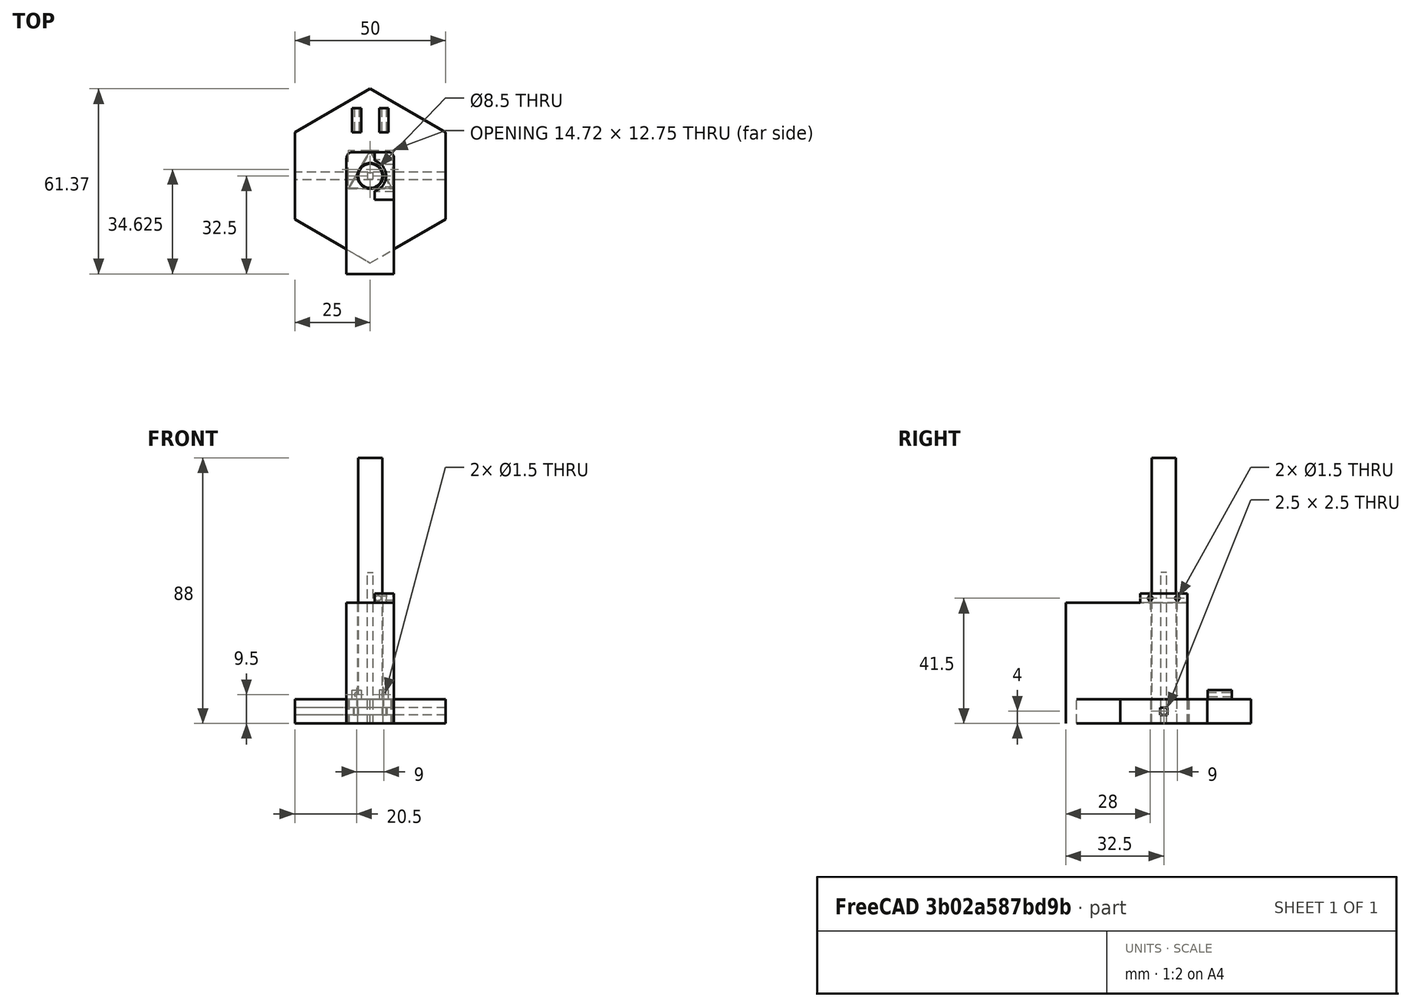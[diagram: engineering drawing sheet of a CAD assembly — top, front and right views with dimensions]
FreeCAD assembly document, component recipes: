
FREECAD ASSEMBLY — COMPONENT RECIPES ("SpringWinder")

This assembly document has 4 components, labeled P0..P3 below (a component is one placed body or linked part). 4 of them carry a construction recipe — the FreeCAD feature program that regenerates the part from scratch, quoted from this document or its linked companion documents; the rest are supplied as boundary geometry only. No exploded tour is included for this assembly.
COMPONENT P0 — recipe-attached ("Handle", modeled in this document).
Construction recipe (the document's own serialized feature program — sketch geometry with constraints, then the solid features built on it; lengths are millimeters unless a unit is written):

FEATURE [Sketcher::SketchObject] Sketch003  label="handle_cylinder_sketch"
  FullyConstrained = true
  MapMode = 5
  Support = -> [XY_Plane004]
  expr: Constraints[18] = <<Specification>>.handle_diameter
  sketch-geometry (7):
    g0: LineSegment StartX=25 StartY=-14.4338 StartZ=0 EndX=25 EndY=14.4338 EndZ=0
    g1: LineSegment StartX=25 StartY=14.4338 StartZ=0 EndX=0 EndY=28.8675 EndZ=0
    g2: LineSegment StartX=0 StartY=28.8675 StartZ=0 EndX=-25 EndY=14.4338 EndZ=0
    g3: LineSegment StartX=-25 StartY=14.4338 StartZ=0 EndX=-25 EndY=-14.4338 EndZ=0
    g4: LineSegment StartX=-25 StartY=-14.4338 StartZ=0 EndX=0 EndY=-28.8675 EndZ=0
    g5: LineSegment StartX=0 StartY=-28.8675 StartZ=0 EndX=25 EndY=-14.4338 EndZ=0
    g6: Circle CenterX=0 CenterY=0 CenterZ=0 NormalX=0 NormalY=0 NormalZ=1 AngleXU=0 Radius=28.8675
  constraints (15):
    c: Coincident(g0,g1)
    c: Coincident(g1,g2)
    c: Coincident(g2,g3)
    c: Coincident(g3,g4)
    c: Coincident(g4,g5)
    c: Coincident(g5,g0)
    c: Equal(g0, g1-g5) x5
    c: PointOnObject(g0,g6)
    c: PointOnObject(g1,g6)
    c: PointOnObject(g2,g6)
    c: PointOnObject(g3,g6)
    c: PointOnObject(g4,g6)
    c: Coincident(g6,g-1)
    c: Symmetric(g3,g0,g-2)
    c: DistanceX(g2,g0) = 50
FEATURE [PartDesign::Pad] Pad002  label="handle_cylinder_pad"
  Direction = (0,0,1)
  Length = 8
  Length2 = 10
  Profile = -> Sketch003
  ReferenceAxis = -> Sketch003 [N_Axis]
  Type = 0
  expr: Length = <<Specification>>.handle_width
FEATURE [PartDesign::CoordinateSystem] Local_CS002  label="handle_pin_hole_cs"
  AttacherType = Attacher::AttachEngine3D
  AttachmentOffset = pos=(25,0,4) rot=(0,0,1;0rad)
  MapMode = 2
  Placement = pos=(25,0,4) rot=(0,0,1;0rad)
  Support = -> [Pad002]
  expr: .AttachmentOffset.Base.x = <<Specification>>.handle_diameter * 0.5
  expr: .AttachmentOffset.Base.z = <<Specification>>.handle_width * 0.5
FEATURE [PartDesign::Plane] DatumPlane001  label="handle_pin_hole_plane"
  Length = 60
  MapMode = 4
  Placement = pos=(25,0,4) rot=(0.57735,0.57735,0.57735;2.0944rad)
  ResizeMode = 0
  Support = -> [Local_CS002]
  Width = 60
FEATURE [Sketcher::SketchObject] Sketch004  label="handle_pin_hole_sketch"
  FullyConstrained = true
  MapMode = 5
  Placement = pos=(25,0,4) rot=(0.57735,0.57735,0.57735;2.0944rad)
  Support = -> [DatumPlane001]
  expr: Constraints[11] = <<Specification>>.fixator_hole_diameter
  sketch-geometry (5):
    g0: LineSegment StartX=-1.25 StartY=-1.25 StartZ=0 EndX=-1.25 EndY=1.25 EndZ=0
    g1: LineSegment StartX=-1.25 StartY=1.25 StartZ=0 EndX=1.25 EndY=1.25 EndZ=0
    g2: LineSegment StartX=1.25 StartY=1.25 StartZ=0 EndX=1.25 EndY=-1.25 EndZ=0
    g3: LineSegment StartX=1.25 StartY=-1.25 StartZ=0 EndX=-1.25 EndY=-1.25 EndZ=0
    g4: GeomPoint X=0 Y=0 Z=0
  constraints (12):
    c: Coincident(g0,g1)
    c: Coincident(g1,g2)
    c: Coincident(g2,g3)
    c: Coincident(g3,g0)
    c: Horizontal(g1)
    c: Horizontal(g3)
    c: Vertical(g0)
    c: Vertical(g2)
    c: Symmetric(g1,g0,g4)
    c: Coincident(g4,g-1)
    c: Equal(g1,g2)
    c: DistanceY(g2,g1) = 2.5
FEATURE [PartDesign::Pocket] Pocket001  label="handle_pin_hole_pocket"
  BaseFeature = -> Pad002
  Direction = (-1,0,0)
  Length = 50
  Length2 = 5
  Profile = -> Sketch004
  ReferenceAxis = -> Sketch004 [N_Axis]
  Type = 1
  expr: Length = <<Specification>>.handle_diameter
FEATURE [Sketcher::SketchObject] Sketch006  label="handle_axis_hole_sketch"
  FullyConstrained = true
  MapMode = 5
  Support = -> [XY_Plane004]
  expr: Constraints[9] = <<Specification>>.inner_radius + <<Parameters>>.big_clearence
  sketch-geometry (4):
    g0: LineSegment StartX=7.36122 StartY=-4.25 StartZ=0 EndX=-9e-16 EndY=8.5 EndZ=0
    g1: LineSegment StartX=-9e-16 StartY=8.5 StartZ=0 EndX=-7.36122 EndY=-4.25 EndZ=0
    g2: LineSegment StartX=-7.36122 StartY=-4.25 StartZ=0 EndX=7.36122 EndY=-4.25 EndZ=0
    g3: Circle CenterX=0 CenterY=0 CenterZ=0 NormalX=0 NormalY=0 NormalZ=1 AngleXU=0 Radius=8.5
  constraints (10):
    c: Coincident(g0,g1)
    c: Coincident(g1,g2)
    c: Coincident(g2,g0)
    c: Equal(g0,g1)
    c: Equal(g0,g2)
    c: PointOnObject(g0,g3)
    c: PointOnObject(g1,g3)
    c: Coincident(g3,g-1)
    c: Symmetric(g1,g0,g-2)
    c: DistanceY(g0,g3) = 4.25
FEATURE [PartDesign::Pocket] Pocket002  label="handle_axis_hole_pocket"
  BaseFeature = -> Pocket001
  Direction = (0,0,-1)
  Length = 5
  Length2 = 5
  Profile = -> Sketch006
  ReferenceAxis = -> Sketch006 [N_Axis]
  Reversed = true
  Type = 1
FEATURE [PartDesign::CoordinateSystem] Local_CS003  label="handle_wire_holder_center_cs"
  AttacherType = Attacher::AttachEngine3D
  AttachmentOffset = pos=(0,14.5,8) rot=(0,0,1;0rad)
  MapMode = 2
  Placement = pos=(0,14.5,8) rot=(0,0,1;0rad)
  Support = -> [Pocket002]
  expr: .AttachmentOffset.Base.y = <<Specification>>.handle_wire_holder_y_offset
  expr: .AttachmentOffset.Base.z = <<Specification>>.handle_width
FEATURE [PartDesign::Plane] DatumPlane002  label="handle_wire_holder_mirror_plane"
  Length = 60
  MapMode = 4
  Placement = pos=(0,14.5,8) rot=(0.57735,0.57735,0.57735;2.0944rad)
  ResizeMode = 0
  Support = -> [Local_CS003]
  Width = 60
FEATURE [PartDesign::CoordinateSystem] Local_CS004  label="handle_wire_holder_cs"
  AttacherType = Attacher::AttachEngine3D
  AttachmentOffset = pos=(0,1.5,4.5) rot=(0,0,1;0rad)
  MapMode = 5
  Placement = pos=(4.5,14.5,9.5) rot=(0.57735,0.57735,0.57735;2.0944rad)
  Support = -> [DatumPlane002]
  expr: .AttachmentOffset.Base.y = <<Specification>>.handle_wire_holder_width * 0.5
  expr: .AttachmentOffset.Base.z = <<Specification>>.handle_wire_holder_x_offset
FEATURE [PartDesign::Plane] DatumPlane003  label="handle_wire_holder_plane"
  Length = 60
  MapMode = 4
  Placement = pos=(4.5,14.5,9.5) rot=(0.57735,0.57735,0.57735;4.18879rad)
  ResizeMode = 0
  Support = -> [Local_CS004]
  Width = 60
FEATURE [Sketcher::SketchObject] Sketch007  label="handle_wire_holder_sketch"
  FullyConstrained = true
  MapMode = 5
  Placement = pos=(4.5,14.5,9.5) rot=(0.57735,0.57735,0.57735;4.18879rad)
  Support = -> [DatumPlane003]
  expr: Constraints[10] = <<Specification>>.handle_wire_holder_width
  expr: Constraints[12] = <<Specification>>.handle_wire_holder_hole_diameter
  sketch-geometry (6):
    g0: LineSegment StartX=-1.5 StartY=-1.5 StartZ=0 EndX=-1.5 EndY=1.5 EndZ=0
    g1: LineSegment StartX=-1.5 StartY=1.5 StartZ=0 EndX=1.5 EndY=1.5 EndZ=0
    g2: LineSegment StartX=1.5 StartY=1.5 StartZ=0 EndX=1.5 EndY=-1.5 EndZ=0
    g3: LineSegment StartX=1.5 StartY=-1.5 StartZ=0 EndX=-1.5 EndY=-1.5 EndZ=0
    g4: GeomPoint X=0 Y=0 Z=0
    g5: Circle CenterX=0 CenterY=0 CenterZ=0 NormalX=0 NormalY=0 NormalZ=1 AngleXU=0 Radius=0.75
  constraints (14):
    c: Coincident(g0,g1)
    c: Coincident(g1,g2)
    c: Coincident(g2,g3)
    c: Coincident(g3,g0)
    c: Horizontal(g1)
    c: Horizontal(g3)
    c: Vertical(g0)
    c: Vertical(g2)
    c: Symmetric(g1,g0,g4)
    c: Coincident(g4,g-1)
    c: DistanceY(g2,g1) = 3
    c: Coincident(g5,g4)
    c: Diameter(g5) = 1.5
    c: Equal(g1,g2)
FEATURE [PartDesign::Pad] Pad004  label="handle_wire_holder_pad"
  BaseFeature = -> Pocket002
  Direction = (0,1,0)
  Length = 8
  Length2 = 10
  Profile = -> Sketch007
  ReferenceAxis = -> Sketch007 [N_Axis]
  Type = 0
  expr: Length = <<Specification>>.handle_wire_holder_length
FEATURE [PartDesign::Mirrored] Mirrored
  MirrorPlane = -> DatumPlane002
FEATURE [PartDesign::MultiTransform] MultiTransform  label="handle_wire_holder_mirror"
  BaseFeature = -> Pad004
  Originals = -> [Pad004]
  Transformations = -> [Mirrored]
FEATURE [PartDesign::Body] Body001  label="handle_body"
  Group = -> [Sketch003,Pad002,Local_CS002,DatumPlane001,Sketch004,Pocket001,Sketch006,Pocket002,Local_CS003,DatumPlane002,Local_CS004,DatumPlane003,Sketch007,Pad004,MultiTransform,Mirrored]
  Origin = -> Origin004
  Tip = -> MultiTransform
COMPONENT P1 — recipe-attached ("FlatAxis", modeled in this document).
Construction recipe (the document's own serialized feature program — sketch geometry with constraints, then the solid features built on it; lengths are millimeters unless a unit is written):

FEATURE [Sketcher::SketchObject] Sketch  label="prism_sketch"
  FullyConstrained = true
  MapMode = 5
  Support = -> [XY_Plane003]
  expr: Constraints[10] = <<Specification>>.inner_radius
  sketch-geometry (4):
    g0: Circle CenterX=0 CenterY=0 CenterZ=0 NormalX=0 NormalY=0 NormalZ=1 AngleXU=0 Radius=8
    g1: LineSegment StartX=-6.9282 StartY=-4 StartZ=0 EndX=8e-15 EndY=8 EndZ=0
    g2: LineSegment StartX=8e-15 StartY=8 StartZ=0 EndX=6.9282 EndY=-4 EndZ=0
    g3: LineSegment StartX=-6.9282 StartY=-4 StartZ=0 EndX=6.9282 EndY=-4 EndZ=0
  constraints (11):
    c: Coincident(g0,g-1)
    c: PointOnObject(g1,g0)
    c: PointOnObject(g3,g0)
    c: PointOnObject(g2,g0)
    c: Coincident(g2,g1)
    c: Coincident(g1,g3)
    c: Coincident(g3,g2)
    c: Equal(g1,g3)
    c: Equal(g2,g3)
    c: Perpendicular(g-2,g3)
    c: DistanceY(g2,g0) = 4
FEATURE [PartDesign::Pad] Pad  label="prism_pad"
  Direction = (0,0,1)
  Length = 8
  Length2 = 10
  Profile = -> Sketch
  ReferenceAxis = -> Sketch [N_Axis]
  Type = 0
  expr: Length = <<Specification>>.handle_width
FEATURE [PartDesign::CoordinateSystem] Local_CS  label="cylinder_cs"
  AttacherType = Attacher::AttachEngine3D
  AttachmentOffset = pos=(0,0,8) rot=(0,0,1;0rad)
  MapMode = 2
  Placement = pos=(0,0,8) rot=(0,0,1;0rad)
  Support = -> [Pad]
  expr: .AttachmentOffset.Base.z = <<Specification>>.handle_width
FEATURE [Sketcher::SketchObject] Sketch001  label="circle"
  FullyConstrained = true
  MapMode = 5
  Placement = pos=(0,0,8) rot=(0,0,1;0rad)
  Support = -> [Local_CS]
  expr: Constraints[1] = <<Specification>>.inner_diameter
  sketch-geometry (1):
    g0: Circle CenterX=0 CenterY=0 CenterZ=0 NormalX=0 NormalY=0 NormalZ=1 AngleXU=0 Radius=4
  constraints (2):
    c: Coincident(g0,g-1)
    c: Diameter(g0) = 8
FEATURE [PartDesign::CoordinateSystem] Local_CS001  label="prism_fixator_hole_cs"
  AttacherType = Attacher::AttachEngine3D
  AttachmentOffset = pos=(6,0,4) rot=(0,0,1;0rad)
  MapMode = 2
  Placement = pos=(6,0,4) rot=(0,0,1;0rad)
  Support = -> [Pad]
  expr: .AttachmentOffset.Base.x = <<Specification>>.fixator_hole_length * 0.5
  expr: .AttachmentOffset.Base.z = <<Specification>>.handle_pin_z_offset
FEATURE [PartDesign::Plane] DatumPlane  label="prism_fixator_hole_plane"
  Length = 60
  MapMode = 4
  Placement = pos=(6,0,4) rot=(0.57735,0.57735,0.57735;2.0944rad)
  ResizeMode = 0
  Support = -> [Local_CS001]
  Width = 60
FEATURE [Sketcher::SketchObject] Sketch002  label="fixator_hole_sketch"
  FullyConstrained = true
  MapMode = 5
  Placement = pos=(6,0,4) rot=(0.57735,0.57735,0.57735;2.0944rad)
  Support = -> [DatumPlane]
  expr: Constraints[11] = <<Specification>>.fixator_hole_diameter
  sketch-geometry (5):
    g0: LineSegment StartX=-1.25 StartY=-1.25 StartZ=0 EndX=-1.25 EndY=1.25 EndZ=0
    g1: LineSegment StartX=-1.25 StartY=1.25 StartZ=0 EndX=1.25 EndY=1.25 EndZ=0
    g2: LineSegment StartX=1.25 StartY=1.25 StartZ=0 EndX=1.25 EndY=-1.25 EndZ=0
    g3: LineSegment StartX=1.25 StartY=-1.25 StartZ=0 EndX=-1.25 EndY=-1.25 EndZ=0
    g4: GeomPoint X=0 Y=0 Z=0
  constraints (12):
    c: Coincident(g0,g1)
    c: Coincident(g1,g2)
    c: Coincident(g2,g3)
    c: Coincident(g3,g0)
    c: Horizontal(g1)
    c: Horizontal(g3)
    c: Vertical(g0)
    c: Vertical(g2)
    c: Symmetric(g1,g0,g4)
    c: Coincident(g4,g-1)
    c: Equal(g1,g2)
    c: DistanceY(g2,g1) = 2.5
FEATURE [PartDesign::Pocket] Pocket  label="prism_fixator_hole_pocket"
  BaseFeature = -> Pad
  Direction = (-1,0,0)
  Length = 12
  Length2 = 5
  Profile = -> Sketch002
  ReferenceAxis = -> Sketch002 [N_Axis]
  Type = 1
  expr: Length = <<Specification>>.fixator_hole_length
FEATURE [PartDesign::Pad] Pad001  label="cylinder_pad"
  BaseFeature = -> Pocket
  Direction = (0,0,1)
  Length = 80
  Length2 = 10
  Profile = -> Sketch001
  ReferenceAxis = -> Sketch001 [N_Axis]
  Type = 0
  expr: Length = <<Specification>>.axis_length
FEATURE [PartDesign::Body] Body  label="axis_body"
  Group = -> [Sketch,Pad,Local_CS001,DatumPlane,Pocket,Sketch002,Local_CS,Sketch001,Pad001]
  Origin = -> Origin003
  Tip = -> Pad001
COMPONENT P2 — recipe-attached ("FlatStator", modeled in this document).
Construction recipe (the document's own serialized feature program — sketch geometry with constraints, then the solid features built on it; lengths are millimeters unless a unit is written):

FEATURE [Sketcher::SketchObject] Sketch008  label="flat_stator_tube_sketch"
  FullyConstrained = true
  MapMode = 5
  Support = -> [XY_Plane008]
  expr: Constraints[0] = <<Specification>>.stator_hole_diameter
  expr: Constraints[19] = <<Specification>>.stator_outside_diameter
  expr: Constraints[20] = <<Specification>>.stator_outside_diameter * 0.5
  expr: Constraints[21] = <<Specification>>.stator_corner_radius
  expr: Constraints[8] = <<Specification>>.stator_height
  sketch-geometry (10):
    g0: Circle CenterX=0 CenterY=0 CenterZ=0 NormalX=0 NormalY=0 NormalZ=1 AngleXU=0 Radius=4.25
    g1: LineSegment StartX=7.875 StartY=0 StartZ=0 EndX=7.875 EndY=-32.5 EndZ=0
    g2: LineSegment StartX=7.875 StartY=-32.5 StartZ=0 EndX=-7.875 EndY=-32.5 EndZ=0
    g3: LineSegment StartX=-7.875 StartY=-32.5 StartZ=0 EndX=-7.875 EndY=0 EndZ=0
    g4: ArcOfCircle CenterX=-5.875 CenterY=5.875 CenterZ=0 NormalX=0 NormalY=0 NormalZ=1 AngleXU=0 Radius=2 StartAngle=1.5708 EndAngle=3.14159
    g5: LineSegment StartX=-5.875 StartY=7.875 StartZ=0 EndX=5.875 EndY=7.875 EndZ=0
    g6: ArcOfCircle CenterX=5.875 CenterY=5.875 CenterZ=0 NormalX=0 NormalY=0 NormalZ=1 AngleXU=0 Radius=2 StartAngle=0 EndAngle=1.5708
    g7: LineSegment StartX=7.875 StartY=5.875 StartZ=0 EndX=7.875 EndY=0 EndZ=0
    g8: LineSegment StartX=-7.875 StartY=0 StartZ=0 EndX=-7.875 EndY=5.875 EndZ=0
    g9: GeomPoint X=-7.875 Y=7.875 Z=0
  constraints (25):
    c: Diameter(g0) = 8.5
    c: Coincident(g0,g-1)
    c: PointOnObject(g1,g-1)
    c: Coincident(g1,g2)
    c: Coincident(g2,g3)
    c: Horizontal(g2)
    c: Vertical(g1)
    c: Vertical(g3)
    c: DistanceY(g1,g0) = 32.5
    c: Tangent(g4,g5) = 1.5708
    c: Tangent(g5,g6) = 1.5708
    c: Tangent(g6,g7) = 1.5708
    c: Tangent(g8,g4) = 1.5708
    c: Horizontal(g5)
    c: Vertical(g7)
    c: Vertical(g8)
    c: Equal(g4,g6)
    c: PointOnObject(g9,g5)
    c: PointOnObject(g9,g8)
    c: DistanceX(g4,g6) = 15.75
    c: DistanceY(g8,g4) = 7.875
    c: Radius(g6) = 2
    c: Coincident(g8,g3)
    c: Coincident(g7,g1)
    c: Symmetric(g3,g1,g0)
FEATURE [PartDesign::Pad] Pad005  label="flat_stator_tube_pad"
  Direction = (0,0,1)
  Length = 40
  Length2 = 10
  Profile = -> Sketch008
  ReferenceAxis = -> Sketch008 [N_Axis]
  Type = 0
  expr: Length = <<Specification>>.stator_length
FEATURE [PartDesign::CoordinateSystem] Local_CS005  label="flat_stator_wire_holder_shield_cs"
  AttacherType = Attacher::AttachEngine3D
  AttachmentOffset = pos=(0,0,40) rot=(0,0,1;0rad)
  MapMode = 2
  Placement = pos=(0,0,40) rot=(0,0,1;0rad)
  Support = -> [Pad005]
  expr: .AttachmentOffset.Base.z = <<Specification>>.stator_length
FEATURE [Sketcher::SketchObject] Sketch009  label="flat_stator_wire_holder_shield_sketch"
  FullyConstrained = true
  MapMode = 5
  Placement = pos=(0,0,40) rot=(0,0,1;0rad)
  Support = -> [Local_CS005]
  expr: Constraints[15] = <<Specification>>.stator_wire_holder_hole_diameter
  expr: Constraints[18] = <<Specification>>.stator_outside_diameter
  expr: Constraints[19] = <<Specification>>.stator_outside_diameter * 0.5
  expr: Constraints[20] = <<Specification>>.stator_corner_radius
  expr: Constraints[2] = <<Specification>>.stator_wire_holder_inside_diameter
  sketch-geometry (8):
    g0: ArcOfCircle CenterX=0 CenterY=0 CenterZ=0 NormalX=0 NormalY=0 NormalZ=1 AngleXU=0 Radius=5.25 StartAngle=5.00214 EndAngle=7.56423
    g1: LineSegment StartX=1.5 StartY=5.03115 StartZ=0 EndX=1.5 EndY=7.875 EndZ=0
    g2: LineSegment StartX=1.5 StartY=-5.03115 StartZ=0 EndX=1.5 EndY=-7.875 EndZ=0
    g3: GeomPoint X=5.25 Y=0 Z=0
    g4: LineSegment StartX=1.5 StartY=7.875 StartZ=0 EndX=5.875 EndY=7.875 EndZ=0
    g5: LineSegment StartX=7.875 StartY=5.875 StartZ=0 EndX=7.875 EndY=-7.875 EndZ=0
    g6: LineSegment StartX=7.875 StartY=-7.875 StartZ=0 EndX=1.5 EndY=-7.875 EndZ=0
    g7: ArcOfCircle CenterX=5.875 CenterY=5.875 CenterZ=0 NormalX=0 NormalY=0 NormalZ=1 AngleXU=0 Radius=2 StartAngle=0 EndAngle=1.5708
  constraints (21):
    c: Coincident(g1,g0)
    c: Coincident(g2,g0)
    c: Diameter(g0) = 10.5
    c: PointOnObject(g3,g0)
    c: PointOnObject(g3,g-1)
    c: Vertical(g2)
    c: Vertical(g1)
    c: Horizontal(g4)
    c: Horizontal(g6)
    c: Vertical(g5)
    c: Coincident(g6,g5)
    c: Coincident(g6,g2)
    c: Coincident(g4,g1)
    c: Coincident(g0,g-1)
    c: Symmetric(g1,g2,g-1)
    c: DistanceX(g0,g0) = 1.5
    c: Tangent(g4,g7) = 1.5708
    c: Tangent(g5,g7) = 1.5708
    c: DistanceY(g5,g4) = 15.75
    c: DistanceX(g0,g5) = 7.875
    c: Radius(g7) = 2
FEATURE [PartDesign::Pad] Pad006  label="flat_stator_wire_holder_shield_pad"
  BaseFeature = -> Pad005
  Direction = (0,0,1)
  Length = 3
  Length2 = 10
  Profile = -> Sketch009
  ReferenceAxis = -> Sketch009 [N_Axis]
  Type = 0
  expr: Length = <<Specification>>.stator_wire_holder_pin_width
FEATURE [PartDesign::CoordinateSystem] Local_CS006  label="flat_stator_wire_holder_pins_center_cs"
  AttacherType = Attacher::AttachEngine3D
  AttachmentOffset = pos=(0,0,1.5) rot=(0,0,1;0rad)
  MapMode = 2
  Placement = pos=(0,0,41.5) rot=(0,0,1;0rad)
  Support = -> [Local_CS005]
  expr: .AttachmentOffset.Base.z = <<Specification>>.stator_wire_holder_pin_width * 0.5
FEATURE [PartDesign::Plane] DatumPlane004  label="flat_stator_wire_holder_pins_mirror_plane"
  Length = 61.5326
  MapMode = 3
  Placement = pos=(0,0,41.5) rot=(1,0,0;1.5708rad)
  ResizeMode = 0
  Support = -> [Local_CS006]
  Width = 78.0326
FEATURE [PartDesign::CoordinateSystem] Local_CS007  label="flat_stator_wire_holder_pins_pos_cs"
  AttacherType = Attacher::AttachEngine3D
  AttachmentOffset = pos=(0,0,4.5) rot=(0,0,1;0rad)
  MapMode = 5
  Placement = pos=(0,-4.5,41.5) rot=(1,0,0;1.5708rad)
  Support = -> [DatumPlane004]
  expr: .AttachmentOffset.Base.z = <<Specification>>.stator_wire_holder_holes_distance * 0.5
FEATURE [PartDesign::Plane] DatumPlane005  label="flat_stator_wire_holder_pins_pos_plane"
  Length = 78.0326
  MapMode = 4
  Placement = pos=(0,-4.5,41.5) rot=(0.707107,0,0.707107;3.14159rad)
  ResizeMode = 0
  Support = -> [Local_CS007]
  Width = 61.5326
FEATURE [Sketcher::SketchObject] Sketch010  label="flat_stator_wire_holder_pins_hole_sketch"
  FullyConstrained = true
  MapMode = 5
  Placement = pos=(0,-4.5,41.5) rot=(0.707107,0,0.707107;3.14159rad)
  Support = -> [DatumPlane005]
  expr: Constraints[1] = <<Specification>>.handle_wire_holder_hole_diameter
  sketch-geometry (1):
    g0: Circle CenterX=0 CenterY=0 CenterZ=0 NormalX=0 NormalY=0 NormalZ=1 AngleXU=0 Radius=0.75
  constraints (2):
    c: Coincident(g0,g-1)
    c: Diameter(g0) = 1.5
FEATURE [PartDesign::Pocket] Pocket003  label="flat_stator_wire_holder_pins_hole_pocket"
  BaseFeature = -> Pad006
  Direction = (-1,0,2e-16)
  Length = 5
  Length2 = 5
  Profile = -> Sketch010
  ReferenceAxis = -> Sketch010 [N_Axis]
  Reversed = true
  Type = 1
FEATURE [PartDesign::Mirrored] Mirrored001
  MirrorPlane = -> DatumPlane004
FEATURE [PartDesign::MultiTransform] MultiTransform001  label="flat_stator_wire_holder_pins_mirror"
  BaseFeature = -> Pocket003
  Originals = -> [Pocket003]
  Transformations = -> [Mirrored001]
FEATURE [PartDesign::Body] Body003  label="flat_stator_body"
  Group = -> [Sketch008,Pad005,Local_CS005,Sketch009,Pad006,Local_CS006,DatumPlane004,Local_CS007,DatumPlane005,Sketch010,Pocket003,MultiTransform001,Mirrored001]
  Origin = -> Origin008
  Tip = -> MultiTransform001
COMPONENT P3 — recipe-attached ("FixatorPin", modeled in this document).
Construction recipe (the document's own serialized feature program — sketch geometry with constraints, then the solid features built on it; lengths are millimeters unless a unit is written):

FEATURE [Sketcher::SketchObject] Sketch005  label="fixator_pin_sketch"
  FullyConstrained = true
  MapMode = 5
  Support = -> [XY_Plane006]
  expr: Constraints[10] = <<Specification>>.fixator_pin_diameter
  sketch-geometry (5):
    g0: LineSegment StartX=-1 StartY=1 StartZ=0 EndX=-1 EndY=-1 EndZ=0
    g1: LineSegment StartX=-1 StartY=-1 StartZ=0 EndX=1 EndY=-1 EndZ=0
    g2: LineSegment StartX=1 StartY=-1 StartZ=0 EndX=1 EndY=1 EndZ=0
    g3: LineSegment StartX=1 StartY=1 StartZ=0 EndX=-1 EndY=1 EndZ=0
    g4: GeomPoint X=0 Y=0 Z=0
  constraints (12):
    c: Coincident(g0,g1)
    c: Coincident(g1,g2)
    c: Coincident(g2,g3)
    c: Coincident(g3,g0)
    c: Horizontal(g1)
    c: Horizontal(g3)
    c: Vertical(g0)
    c: Vertical(g2)
    c: Symmetric(g1,g0,g4)
    c: Equal(g3,g2)
    c: DistanceY(g1,g2) = 2
    c: Coincident(g4,g-1)
FEATURE [PartDesign::Pad] Pad003  label="fixator_pin_pad"
  Direction = (0,0,1)
  Length = 50
  Length2 = 10
  Profile = -> Sketch005
  ReferenceAxis = -> Sketch005 [N_Axis]
  Type = 0
  expr: Length = <<Specification>>.handle_diameter
FEATURE [PartDesign::Body] Body002  label="fixator_pin_body"
  Group = -> [Sketch005,Pad003]
  Origin = -> Origin006
  Tip = -> Pad003
PROVENANCE & LICENSES
A FreeCAD (.FCStd) document from a public repository crawl; recipes are the document's own serialized feature recipes (and, for linked parts, companion documents' recipes).
License: mit.
